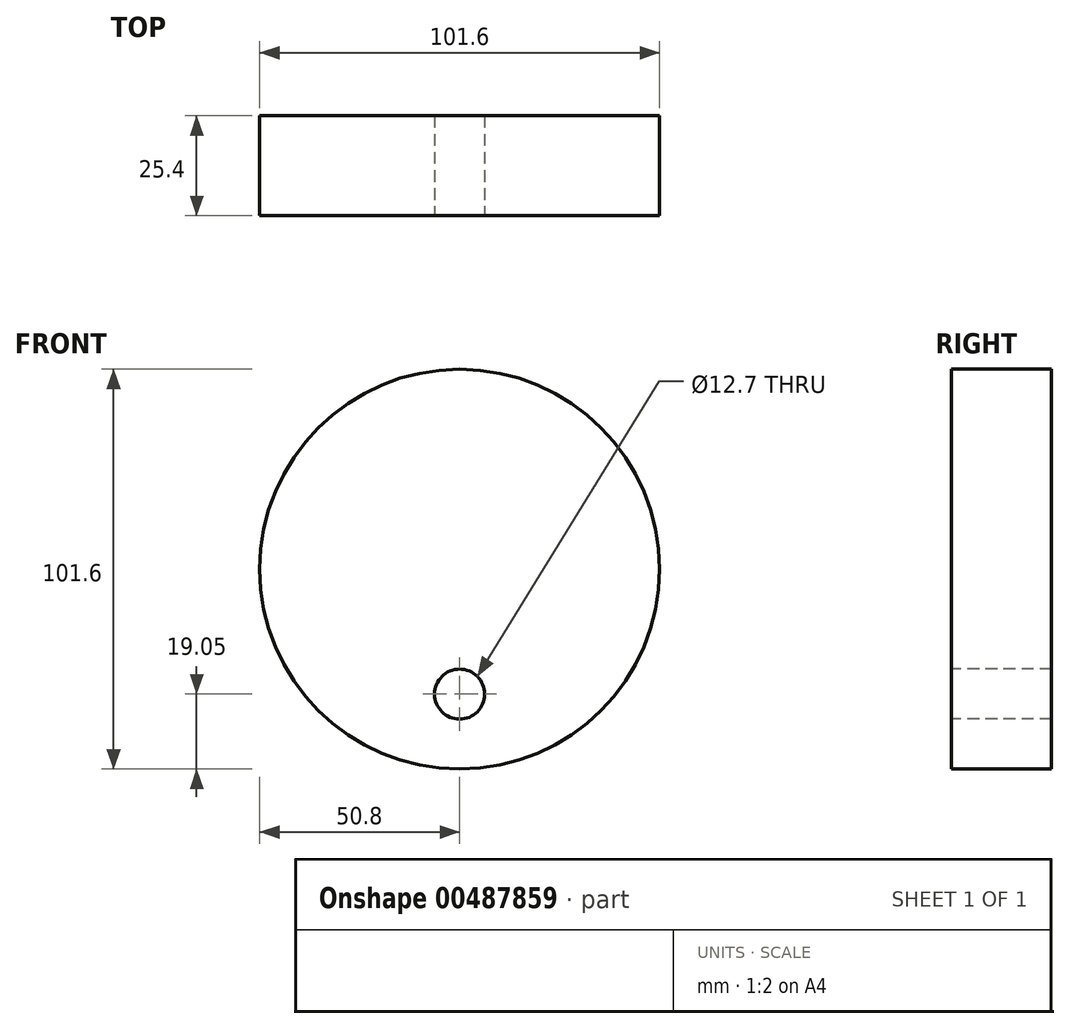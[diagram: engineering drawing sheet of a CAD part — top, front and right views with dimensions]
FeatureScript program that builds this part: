
annotation { "Feature Type Name" : "Feature", "Feature Type Description" : "" }
export const myFeature = defineFeature(function(context is Context, id is Id, definition is map)
    precondition{}
    {
        {
            var Q0;
            Q0=qCreatedBy(makeId("Front.planeOp"),FACE);
            var sketch = newSketch(context, id + "F0", { "sketchPlane" : qUnion([Q0])});
            skCircle(sketch, "E0", {"center": v(0, 0) * mm, "radius": 50.8 * mm});
            skSolve(sketch);
        }
        {
            var Q0;
            Q0 = qSketchRegion(id + "F0", true);
            extrude(context, id + "F1", {"entities" : qUnion([Q0]), "depth" : 25.4 * mm});
        }
        {
            var Q0;
            Q0=makeQuery(id+"F1.opExtrude","CAP_FACE",FACE,{"disambiguationData":[OSD([sQuery(id+"F0.wireOp",EDGE,"E0")])],"isStart":false});
            var sketch = newSketch(context, id + "F2", { "sketchPlane" : qUnion([Q0])});
            skCircle(sketch, "E1", {"center": v(0, 0) * mm, "radius": 31.75 * mm, "construction": true});
            skCircle(sketch, "E2", {"center": v(0, -31.75) * mm, "radius": 6.35 * mm});
            skSolve(sketch);
        }
        {
            var Q0;
            Q0 = qSketchRegion(id + "F2", true);
            var Q1;
            Q1=makeQuery(id+"F2.imprint","IMPRINT",FACE,{"disambiguationData":[TD([[makeQuery(id+"F2.imprint","IMPRINT",EDGE,{"derivedFrom":sQuery(id+"F2.wireOp",EDGE,"E2")}),1.0]])]});
            extrude(context, id + "F3", {"entities" : qUnion([Q0, Q1]), "operationType" : NewBodyOperationType.REMOVE, "oppositeDirection" : true, "depth" : 25.4 * mm});
        }
        {
            var Q0;
            Q0=makeQuery(id+"F1.opExtrude","CAP_FACE",FACE,{"disambiguationData":[OSD([sQuery(id+"F0.wireOp",EDGE,"E0")])],"isStart":false});
            var sketch = newSketch(context, id + "F4", { "sketchPlane" : qUnion([Q0])});
            skCircle(sketch, "E3", {"center": v(0, 0) * mm, "radius": 31.75 * mm, "construction": true});
            skSolve(sketch);
        }
    });
